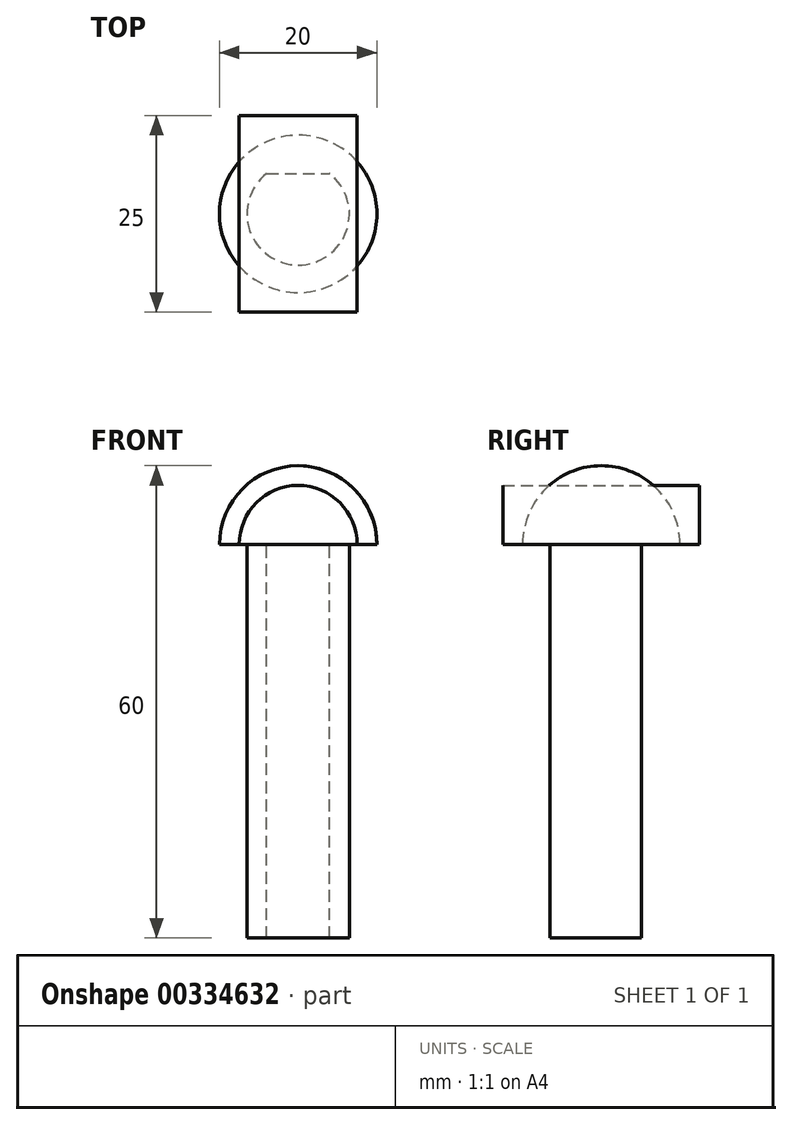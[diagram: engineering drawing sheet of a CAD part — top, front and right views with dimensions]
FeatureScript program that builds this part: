
annotation { "Feature Type Name" : "Feature", "Feature Type Description" : "" }
export const myFeature = defineFeature(function(context is Context, id is Id, definition is map)
    precondition{}
    {
        {
            var Q0;
            Q0=qCreatedBy(makeId("Front.planeOp"),FACE);
            var sketch = newSketch(context, id + "F0", { "sketchPlane" : qUnion([Q0])});
            skArc(sketch, "E0", {"start": v(0, 10) * mm, "mid": v(-7.07, 7.07) * mm, "end": v(-10, 0) * mm});
            skLineSegment(sketch, "E1", {"start": v(0, 10) * mm, "end": v(0, 0) * mm});
            skLineSegment(sketch, "E2", {"start": v(-10, 0) * mm, "end": v(0, 0) * mm});
            skSolve(sketch);
        }
        {
            var Q0;
            Q0=makeQuery(id+"F0.imprint","IMPRINT",FACE,{"disambiguationData":[TD([[makeQuery(id+"F0.imprint","IMPRINT",EDGE,{"derivedFrom":sQuery(id+"F0.wireOp",EDGE,"E0")}),1.0]])]});
            var Q1;
            Q1=sQuery(id+"F0.wireOp",EDGE,"E1");
            revolve(context, id + "F1", {"entities" : qUnion([Q0]), "axis" : qUnion([Q1]), "revolveType" : RevolveType.FULL});
        }
        {
            var Q0;
            Q0=qCreatedBy(makeId("Top.planeOp"),FACE);
            var sketch = newSketch(context, id + "F2", { "sketchPlane" : qUnion([Q0])});
            skArc(sketch, "E3", {"start": v(-4, 5.12) * mm, "mid": v(0, -6.5) * mm, "end": v(4, 5.12) * mm});
            skLineSegment(sketch, "E4", {"start": v(-4, 5.12) * mm, "end": v(4, 5.12) * mm});
            skSolve(sketch);
        }
        {
            var Q0;
            Q0 = qSketchRegion(id + "F2", true);
            extrude(context, id + "F3", {"entities" : qUnion([Q0]), "oppositeDirection" : true, "depth" : 50 * mm});
        }
        {
            var Q0;
            Q0=qCreatedBy(makeId("Front.planeOp"),FACE);
            var sketch = newSketch(context, id + "F4", { "sketchPlane" : qUnion([Q0])});
            skArc(sketch, "E5", {"start": v(0, 7.5) * mm, "mid": v(-5.3, 5.3) * mm, "end": v(-7.5, 0) * mm});
            skArc(sketch, "E6", {"start": v(7.5, 0) * mm, "mid": v(5.3, 5.3) * mm, "end": v(0, 7.5) * mm});
            skLineSegment(sketch, "E7", {"start": v(-7.5, 0) * mm, "end": v(7.5, 0) * mm});
            skSolve(sketch);
        }
        {
            var Q0;
            Q0=makeQuery(id+"F4.imprint","IMPRINT",FACE,{"disambiguationData":[TD([[makeQuery(id+"F4.imprint","IMPRINT",EDGE,{"derivedFrom":sQuery(id+"F4.wireOp",EDGE,"E5")}),1.0]])]});
            extrude(context, id + "F5", {"entities" : qUnion([Q0]), "endBound" : BoundingType.SYMMETRIC, "depth" : 25 * mm});
        }
    });
